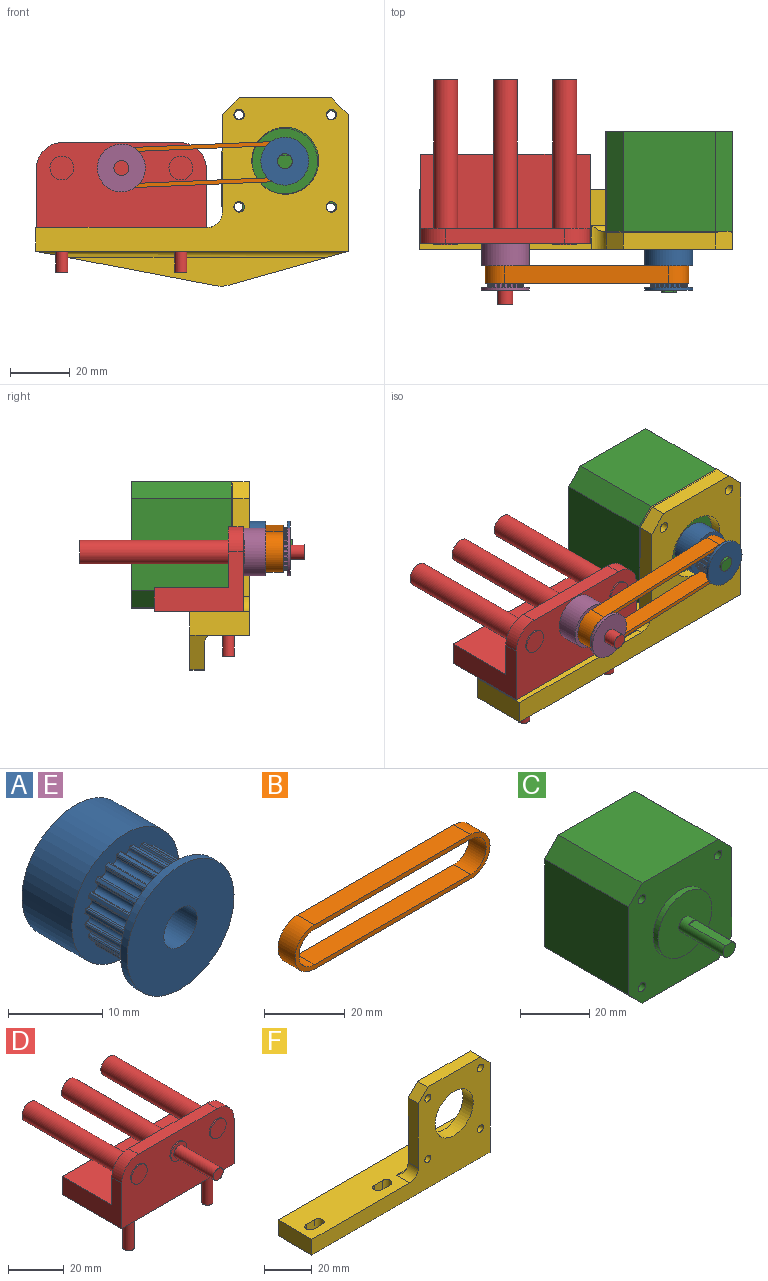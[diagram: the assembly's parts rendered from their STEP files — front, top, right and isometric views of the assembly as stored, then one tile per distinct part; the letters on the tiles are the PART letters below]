
ASSEMBLY  parts=6 mates=3
PART A: 127 faces, bbox 16.1x15.8x16.1 mm
  f0: cylinder r=2.5mm len=15.8mm, axis (0,1,0), area 248.2mm2, adj f3,f125
  f1: cylinder r=8.05mm len=16.1mm, axis (0,1,0), area 379.3mm2, adj f2,f3
  f2: plane 16.1x16.1mm, normal (0,-1,0), area 100.5mm2, adj f1,f4,f5,f6,f7,f8,f9,f10
  f3: plane 16.1x16.1mm, normal (0,1,0), area 183.9mm2, adj f0,f1
  f4: cylinder r=1mm len=7.3mm, axis (0,1,0), area 1.9mm2, adj f2,f5,f123,f126
  f5: cylinder r=0.15mm len=7.3mm, axis (0,1,0), area 1.7mm2, adj f2,f4,f6,f126
  f6: cylinder r=6.12mm len=7.3mm, axis (0,1,0), area 3mm2, adj f2,f5,f7,f126
  f7: cylinder r=0.15mm len=7.3mm, axis (0,1,0), area 1.7mm2, adj f2,f6,f8,f126
  f8: cylinder r=1mm len=7.3mm, axis (0,1,0), area 1.9mm2, adj f2,f7,f9,f126
  f9: cylinder r=0.56mm len=7.3mm, axis (0,1,0), area 9.5mm2, adj f2,f8,f10,f126
  f10: cylinder r=1mm len=7.3mm, axis (0,1,0), area 1.9mm2, adj f2,f9,f11,f126
  f11: cylinder r=0.15mm len=7.3mm, axis (0,1,0), area 1.7mm2, adj f2,f10,f12,f126
  f12: cylinder r=6.12mm len=7.3mm, axis (0,1,0), area 3mm2, adj f2,f11,f13,f126
  f13: cylinder r=0.15mm len=7.3mm, axis (0,1,0), area 1.7mm2, adj f2,f12,f14,f126
  f14: cylinder r=1mm len=7.3mm, axis (0,1,0), area 1.9mm2, adj f2,f13,f15,f126
  f15: cylinder r=0.56mm len=7.3mm, axis (0,1,0), area 9.5mm2, adj f2,f14,f16,f126
  f16: cylinder r=1mm len=7.3mm, axis (0,1,0), area 1.9mm2, adj f2,f15,f17,f126
  f17: cylinder r=0.15mm len=7.3mm, axis (0,1,0), area 1.7mm2, adj f2,f16,f18,f126
  f18: cylinder r=6.12mm len=7.3mm, axis (0,1,0), area 3mm2, adj f2,f17,f19,f126
  f19: cylinder r=0.15mm len=7.3mm, axis (0,1,0), area 1.7mm2, adj f2,f18,f20,f126
  f20: cylinder r=1mm len=7.3mm, axis (0,1,0), area 1.9mm2, adj f2,f19,f21,f126
  f21: cylinder r=0.56mm len=7.3mm, axis (0,1,0), area 9.5mm2, adj f2,f20,f22,f126
  f22: cylinder r=1mm len=7.3mm, axis (0,1,0), area 1.9mm2, adj f2,f21,f23,f126
  f23: cylinder r=0.15mm len=7.3mm, axis (0,1,0), area 1.7mm2, adj f2,f22,f24,f126
  f24: cylinder r=6.12mm len=7.3mm, axis (0,1,0), area 3mm2, adj f2,f23,f25,f126
  f25: cylinder r=0.15mm len=7.3mm, axis (0,1,0), area 1.7mm2, adj f2,f24,f26,f126
  f26: cylinder r=1mm len=7.3mm, axis (0,1,0), area 1.9mm2, adj f2,f25,f27,f126
  f27: cylinder r=0.56mm len=7.3mm, axis (0,1,0), area 9.5mm2, adj f2,f26,f28,f126
  f28: cylinder r=1mm len=7.3mm, axis (0,1,0), area 1.9mm2, adj f2,f27,f29,f126
  f29: cylinder r=0.15mm len=7.3mm, axis (0,1,0), area 1.7mm2, adj f2,f28,f30,f126
  f30: cylinder r=6.12mm len=7.3mm, axis (0,1,0), area 3mm2, adj f2,f29,f31,f126
  f31: cylinder r=0.15mm len=7.3mm, axis (0,1,0), area 1.7mm2, adj f2,f30,f32,f126
  f32: cylinder r=1mm len=7.3mm, axis (0,1,0), area 1.9mm2, adj f2,f31,f33,f126
  f33: cylinder r=0.56mm len=7.3mm, axis (0,1,0), area 9.5mm2, adj f2,f32,f34,f126
  f34: cylinder r=1mm len=7.3mm, axis (0,1,0), area 1.9mm2, adj f2,f33,f35,f126
  f35: cylinder r=0.15mm len=7.3mm, axis (0,1,0), area 1.7mm2, adj f2,f34,f36,f126
  f36: cylinder r=6.12mm len=7.3mm, axis (0,1,0), area 3mm2, adj f2,f35,f37,f126
  f37: cylinder r=0.15mm len=7.3mm, axis (0,1,0), area 1.7mm2, adj f2,f36,f38,f126
  f38: cylinder r=1mm len=7.3mm, axis (0,1,0), area 1.9mm2, adj f2,f37,f39,f126
  f39: cylinder r=0.56mm len=7.3mm, axis (0,1,0), area 9.5mm2, adj f2,f38,f40,f126
  f40: cylinder r=1mm len=7.3mm, axis (0,1,0), area 1.9mm2, adj f2,f39,f41,f126
  f41: cylinder r=0.15mm len=7.3mm, axis (0,1,0), area 1.7mm2, adj f2,f40,f42,f126
  f42: cylinder r=6.12mm len=7.3mm, axis (0,1,0), area 3mm2, adj f2,f41,f43,f126
  f43: cylinder r=0.15mm len=7.3mm, axis (0,1,0), area 1.7mm2, adj f2,f42,f44,f126
  f44: cylinder r=1mm len=7.3mm, axis (0,1,0), area 1.9mm2, adj f2,f43,f45,f126
  f45: cylinder r=0.56mm len=7.3mm, axis (0,1,0), area 9.5mm2, adj f2,f44,f46,f126
  f46: cylinder r=1mm len=7.3mm, axis (0,1,0), area 1.9mm2, adj f2,f45,f47,f126
  f47: cylinder r=0.15mm len=7.3mm, axis (0,1,0), area 1.7mm2, adj f2,f46,f48,f126
  f48: cylinder r=6.12mm len=7.3mm, axis (0,1,0), area 3mm2, adj f2,f47,f49,f126
  f49: cylinder r=0.15mm len=7.3mm, axis (0,1,0), area 1.7mm2, adj f2,f48,f50,f126
  f50: cylinder r=1mm len=7.3mm, axis (0,1,0), area 1.9mm2, adj f2,f49,f51,f126
  f51: cylinder r=0.56mm len=7.3mm, axis (0,1,0), area 9.5mm2, adj f2,f50,f52,f126
  f52: cylinder r=1mm len=7.3mm, axis (0,1,0), area 1.9mm2, adj f2,f51,f53,f126
  f53: cylinder r=0.15mm len=7.3mm, axis (0,1,0), area 1.7mm2, adj f2,f52,f54,f126
  f54: cylinder r=6.12mm len=7.3mm, axis (0,1,0), area 3mm2, adj f2,f53,f55,f126
  f55: cylinder r=0.15mm len=7.3mm, axis (0,1,0), area 1.7mm2, adj f2,f54,f56,f126
  f56: cylinder r=1mm len=7.3mm, axis (0,1,0), area 1.9mm2, adj f2,f55,f57,f126
  f57: cylinder r=0.56mm len=7.3mm, axis (0,1,0), area 9.5mm2, adj f2,f56,f58,f126
  f58: cylinder r=1mm len=7.3mm, axis (0,1,0), area 1.9mm2, adj f2,f57,f59,f126
  f59: cylinder r=0.15mm len=7.3mm, axis (0,1,0), area 1.7mm2, adj f2,f58,f60,f126
  f60: cylinder r=6.12mm len=7.3mm, axis (0,1,0), area 3mm2, adj f2,f59,f61,f126
  f61: cylinder r=0.15mm len=7.3mm, axis (0,1,0), area 1.7mm2, adj f2,f60,f62,f126
  f62: cylinder r=1mm len=7.3mm, axis (0,1,0), area 1.9mm2, adj f2,f61,f63,f126
  f63: cylinder r=0.56mm len=7.3mm, axis (0,1,0), area 9.5mm2, adj f2,f62,f64,f126
  f64: cylinder r=1mm len=7.3mm, axis (0,1,0), area 1.9mm2, adj f2,f63,f65,f126
  f65: cylinder r=0.15mm len=7.3mm, axis (0,1,0), area 1.7mm2, adj f2,f64,f66,f126
  f66: cylinder r=6.12mm len=7.3mm, axis (0,1,0), area 3mm2, adj f2,f65,f67,f126
  f67: cylinder r=0.15mm len=7.3mm, axis (0,1,0), area 1.7mm2, adj f2,f66,f68,f126
  f68: cylinder r=1mm len=7.3mm, axis (0,1,0), area 1.9mm2, adj f2,f67,f69,f126
  f69: cylinder r=0.56mm len=7.3mm, axis (0,1,0), area 9.5mm2, adj f2,f68,f70,f126
  f70: cylinder r=1mm len=7.3mm, axis (0,1,0), area 1.9mm2, adj f2,f69,f71,f126
  f71: cylinder r=0.15mm len=7.3mm, axis (0,1,0), area 1.7mm2, adj f2,f70,f72,f126
  f72: cylinder r=6.12mm len=7.3mm, axis (0,1,0), area 3mm2, adj f2,f71,f73,f126
  f73: cylinder r=0.15mm len=7.3mm, axis (0,1,0), area 1.7mm2, adj f2,f72,f74,f126
  f74: cylinder r=1mm len=7.3mm, axis (0,1,0), area 1.9mm2, adj f2,f73,f75,f126
  f75: cylinder r=0.56mm len=7.3mm, axis (0,1,0), area 9.5mm2, adj f2,f74,f76,f126
  f76: cylinder r=1mm len=7.3mm, axis (0,1,0), area 1.9mm2, adj f2,f75,f77,f126
  f77: cylinder r=0.15mm len=7.3mm, axis (0,1,0), area 1.7mm2, adj f2,f76,f78,f126
  f78: cylinder r=6.12mm len=7.3mm, axis (0,1,0), area 3mm2, adj f2,f77,f79,f126
  f79: cylinder r=0.15mm len=7.3mm, axis (0,1,0), area 1.7mm2, adj f2,f78,f80,f126
  f80: cylinder r=1mm len=7.3mm, axis (0,1,0), area 1.9mm2, adj f2,f79,f81,f126
  f81: cylinder r=0.56mm len=7.3mm, axis (0,1,0), area 9.5mm2, adj f2,f80,f82,f126
  f82: cylinder r=1mm len=7.3mm, axis (0,1,0), area 1.9mm2, adj f2,f81,f83,f126
  f83: cylinder r=0.15mm len=7.3mm, axis (0,1,0), area 1.7mm2, adj f2,f82,f84,f126
  f84: cylinder r=6.12mm len=7.3mm, axis (0,1,0), area 3mm2, adj f2,f83,f85,f126
  f85: cylinder r=0.15mm len=7.3mm, axis (0,1,0), area 1.7mm2, adj f2,f84,f86,f126
  f86: cylinder r=1mm len=7.3mm, axis (0,1,0), area 1.9mm2, adj f2,f85,f87,f126
  f87: cylinder r=0.56mm len=7.3mm, axis (0,1,0), area 9.5mm2, adj f2,f86,f88,f126
  f88: cylinder r=1mm len=7.3mm, axis (0,1,0), area 1.9mm2, adj f2,f87,f89,f126
  f89: cylinder r=0.15mm len=7.3mm, axis (0,1,0), area 1.7mm2, adj f2,f88,f90,f126
  f90: cylinder r=6.12mm len=7.3mm, axis (0,1,0), area 3mm2, adj f2,f89,f91,f126
  f91: cylinder r=0.15mm len=7.3mm, axis (0,1,0), area 1.7mm2, adj f2,f90,f92,f126
  f92: cylinder r=1mm len=7.3mm, axis (0,1,0), area 1.9mm2, adj f2,f91,f93,f126
  f93: cylinder r=0.56mm len=7.3mm, axis (0,1,0), area 9.5mm2, adj f2,f92,f94,f126
  f94: cylinder r=1mm len=7.3mm, axis (0,1,0), area 1.9mm2, adj f2,f93,f95,f126
  f95: cylinder r=0.15mm len=7.3mm, axis (0,1,0), area 1.7mm2, adj f2,f94,f96,f126
  f96: cylinder r=6.12mm len=7.3mm, axis (0,1,0), area 3mm2, adj f2,f95,f97,f126
  f97: cylinder r=0.15mm len=7.3mm, axis (0,1,0), area 1.7mm2, adj f2,f96,f98,f126
  f98: cylinder r=1mm len=7.3mm, axis (0,1,0), area 1.9mm2, adj f2,f97,f99,f126
  f99: cylinder r=0.56mm len=7.3mm, axis (0,1,0), area 9.5mm2, adj f2,f98,f100,f126
  f100: cylinder r=1mm len=7.3mm, axis (0,1,0), area 1.9mm2, adj f2,f99,f101,f126
  f101: cylinder r=0.15mm len=7.3mm, axis (0,1,0), area 1.7mm2, adj f2,f100,f102,f126
  f102: cylinder r=6.12mm len=7.3mm, axis (0,1,0), area 3mm2, adj f2,f101,f103,f126
  f103: cylinder r=0.15mm len=7.3mm, axis (0,1,0), area 1.7mm2, adj f2,f102,f104,f126
  f104: cylinder r=1mm len=7.3mm, axis (0,1,0), area 1.9mm2, adj f2,f103,f105,f126
  f105: cylinder r=0.56mm len=7.3mm, axis (0,1,0), area 9.5mm2, adj f2,f104,f106,f126
  f106: cylinder r=1mm len=7.3mm, axis (0,1,0), area 1.9mm2, adj f2,f105,f107,f126
  f107: cylinder r=0.15mm len=7.3mm, axis (0,1,0), area 1.7mm2, adj f2,f106,f108,f126
  f108: cylinder r=6.12mm len=7.3mm, axis (0,1,0), area 3mm2, adj f2,f107,f109,f126
  f109: cylinder r=0.15mm len=7.3mm, axis (0,1,0), area 1.7mm2, adj f2,f108,f110,f126
  f110: cylinder r=1mm len=7.3mm, axis (0,1,0), area 1.9mm2, adj f2,f109,f111,f126
  f111: cylinder r=0.56mm len=7.3mm, axis (0,1,0), area 9.5mm2, adj f2,f110,f112,f126
  f112: cylinder r=1mm len=7.3mm, axis (0,1,0), area 1.9mm2, adj f2,f111,f113,f126
  f113: cylinder r=0.15mm len=7.3mm, axis (0,1,0), area 1.7mm2, adj f2,f112,f114,f126
  f114: cylinder r=6.12mm len=7.3mm, axis (0,1,0), area 3mm2, adj f2,f113,f115,f126
  f115: cylinder r=0.15mm len=7.3mm, axis (0,1,0), area 1.7mm2, adj f2,f114,f116,f126
  f116: cylinder r=1mm len=7.3mm, axis (0,1,0), area 1.9mm2, adj f2,f115,f117,f126
  f117: cylinder r=0.56mm len=7.3mm, axis (0,1,0), area 9.5mm2, adj f2,f116,f118,f126
  f118: cylinder r=1mm len=7.3mm, axis (0,1,0), area 1.9mm2, adj f2,f117,f119,f126
  f119: cylinder r=0.15mm len=7.3mm, axis (0,1,0), area 1.7mm2, adj f2,f118,f120,f126
  f120: cylinder r=6.12mm len=7.3mm, axis (0,1,0), area 3mm2, adj f2,f119,f121,f126
  f121: cylinder r=0.15mm len=7.3mm, axis (0,1,0), area 1.7mm2, adj f2,f120,f122,f126
  f122: cylinder r=1mm len=7.3mm, axis (0,1,0), area 1.9mm2, adj f2,f121,f123,f126
  f123: cylinder r=0.56mm len=7.3mm, axis (0,1,0), area 9.5mm2, adj f2,f4,f122,f126
  f124: cylinder r=8.05mm len=16.1mm, axis (0,1,0), area 50.6mm2, adj f125,f126
  f125: plane 16.1x16.1mm, normal (0,-1,0), area 183.9mm2, adj f0,f124
  f126: plane 16.1x16.1mm, normal (0,1,0), area 100.5mm2, adj f4,f5,f6,f7,f8,f9,f10,f11
PART B: 10 faces, bbox 68.5x6x13.5 mm
  f0: plane 55x6mm, normal (0,0,1), area 330mm2, adj f1,f7,f8,f9
  f1: cylinder r=5.37mm len=10.73mm, axis (0,1,0), area 101.1mm2, adj f0,f2,f8,f9
  f2: plane 55x6mm, normal (0,0,-1), area 330mm2, adj f1,f7,f8,f9
  f3: cylinder r=6.75mm len=13.49mm, axis (0,1,0), area 127.1mm2, adj f4,f6,f8,f9
  f4: plane 55x6mm, normal (0,0,-1), area 330mm2, adj f3,f5,f8,f9
  f5: cylinder r=6.75mm len=13.49mm, axis (0,1,0), area 127.1mm2, adj f4,f6,f8,f9
  f6: plane 55x6mm, normal (0,0,1), area 330mm2, adj f3,f5,f8,f9
  f7: cylinder r=5.37mm len=10.73mm, axis (0,1,0), area 101.1mm2, adj f0,f2,f8,f9
  f8: plane 68.49x13.49mm, normal (0,-1,0), area 204.3mm2, adj f0,f1,f2,f3,f4,f5,f6,f7
  f9: plane 68.49x13.49mm, normal (0,1,0), area 204.3mm2, adj f0,f1,f2,f3,f4,f5,f6,f7
PART C: 20 faces, bbox 42.3x54x42.3 mm
  f0: cylinder r=11mm len=22mm, axis (0,1,0), area 138.2mm2, adj f1,f18
  f1: plane 22x22mm, normal (0,-1,0), area 360.5mm2, adj f0,f3
  f2: plane 15x3mm, normal (0,0,1), area 45mm2, adj f3,f4,f5
  f3: cylinder r=2.5mm len=18mm, axis (0,1,0), area 234.5mm2, adj f1,f2,f4,f5
  f4: plane 5x4.5mm, normal (0,-1,0), area 18.6mm2, adj f2,f3
  f5: plane 3x0.5mm, normal (0,-1,0), area 1mm2, adj f2,f3
  f6: plane 34x31mm, normal (0,0,-1), area 1054mm2, adj f7,f16,f18,f19
  f7: plane 34x5.65mm, normal (0.71,0,-0.71), area 271.7mm2, adj f6,f8,f18,f19
  f8: plane 34x31mm, normal (1,0,0), area 1054mm2, adj f7,f9,f18,f19
  f9: plane 34x5.65mm, normal (0.71,0,0.71), area 271.7mm2, adj f8,f10,f18,f19
  f10: plane 34x31mm, normal (0,0,1), area 1054mm2, adj f9,f11,f18,f19
  f11: plane 34x5.65mm, normal (-0.71,0,0.71), area 271.7mm2, adj f10,f12,f18,f19
  f12: plane 34x31mm, normal (-1,0,0), area 1054mm2, adj f11,f16,f18,f19
  f13: cylinder r=1.5mm len=34mm, axis (0,-1,0), area 320.4mm2, adj f18,f19
  f14: cylinder r=1.5mm len=34mm, axis (0,-1,0), area 320.4mm2, adj f18,f19
  f15: cylinder r=1.5mm len=34mm, axis (0,-1,0), area 320.4mm2, adj f18,f19
  f16: plane 34x5.65mm, normal (-0.71,0,-0.71), area 271.7mm2, adj f6,f12,f18,f19
  f17: cylinder r=1.5mm len=34mm, axis (0,-1,0), area 320.4mm2, adj f18,f19
  f18: plane 42.3x42.3mm, normal (0,-1,0), area 1317mm2, adj f0,f6,f7,f8,f9,f10,f11,f12
  f19: plane 42.3x42.3mm, normal (0,1,0), area 1697.2mm2, adj f6,f7,f8,f9,f10,f11,f12,f13
PART D: 28 faces, bbox 57x75.5x43.5 mm
  f0: plane 57x30mm, normal (0,0,-1), area 1684.9mm2, adj f1,f5,f6,f21,f22,f24
  f1: plane 30x20mm, normal (1,0,0), area 300mm2, adj f0,f2,f6,f7,f20,f21
  f2: cylinder r=8.5mm len=8.5mm, axis (0,1,0), area 66.8mm2, adj f1,f3,f6,f7
  f3: plane 40x5mm, normal (0,0,1), area 200mm2, adj f2,f4,f6,f7
  f4: cylinder r=8.5mm len=8.5mm, axis (0,1,0), area 66.8mm2, adj f3,f5,f6,f7
  f5: plane 30x20mm, normal (-1,0,0), area 300mm2, adj f0,f4,f6,f7,f20,f21
  f6: plane 57x28.5mm, normal (0,-1,0), area 1442.7mm2, adj f0,f1,f2,f3,f4,f5,f10,f14
  f7: plane 57x20.5mm, normal (0,1,0), area 986.7mm2, adj f1,f2,f3,f4,f5,f9,f13,f17
  f8: plane 8x8mm, normal (0,1,0), area 50.3mm2, adj f9
  f9: cylinder r=4mm len=50mm, axis (0,-1,0), area 1256.6mm2, adj f7,f8
  f10: cylinder r=4mm len=8mm, axis (0,-1,0), area 12.6mm2, adj f6,f11
  f11: plane 8x8mm, normal (0,-1,0), area 30.6mm2, adj f10,f26
  f12: plane 8x8mm, normal (0,1,0), area 50.3mm2, adj f13
  f13: cylinder r=4mm len=50mm, axis (0,-1,0), area 1256.6mm2, adj f7,f12
  f14: cylinder r=4mm len=8mm, axis (0,-1,0), area 12.6mm2, adj f6,f15
  f15: plane 8x8mm, normal (0,-1,0), area 50.3mm2, adj f14
  f16: plane 8x8mm, normal (0,1,0), area 50.3mm2, adj f17
  f17: cylinder r=4mm len=50mm, axis (0,-1,0), area 1256.6mm2, adj f7,f16
  f18: cylinder r=4mm len=8mm, axis (0,-1,0), area 12.6mm2, adj f6,f19
  f19: plane 8x8mm, normal (0,-1,0), area 50.3mm2, adj f18
  f20: plane 57x25mm, normal (0,0,1), area 1425mm2, adj f1,f5,f7,f21
  f21: plane 57x8mm, normal (0,1,0), area 456mm2, adj f0,f1,f5,f20
  f22: cylinder r=2mm len=15mm, axis (0,0,1), area 188.5mm2, adj f0,f23
  f23: plane 4x4mm, normal (0,0,-1), area 12.6mm2, adj f22
  f24: cylinder r=2mm len=15mm, axis (0,0,1), area 188.5mm2, adj f0,f25
  f25: plane 4x4mm, normal (0,0,-1), area 12.6mm2, adj f24
  f26: cylinder r=2.5mm len=20mm, axis (0,1,0), area 314.2mm2, adj f11,f27
  f27: plane 5x5mm, normal (0,-1,0), area 19.6mm2, adj f26
PART E: same geometry as A
PART F: 31 faces, bbox 105x20x63.3 mm
  f0: plane 105x13mm, normal (0,0,-1), area 1288.2mm2, adj f3,f5,f6,f7,f8,f9,f10,f11
  f1: plane 32.93x6mm, normal (-1,0,0), area 197.6mm2, adj f16,f22,f23,f24
  f2: plane 105x20mm, normal (0,0,1), area 1644.8mm2, adj f3,f4,f5,f6,f7,f8,f9,f10
  f3: plane 45.93x20mm, normal (1,0,0), area 388.4mm2, adj f0,f2,f4,f14,f22,f23,f25,f26
  f4: plane 105x19.73mm, normal (0,1,0), area 1469.6mm2, adj f2,f3,f13,f26,f27,f28
  f5: cylinder r=2.25mm len=8mm, axis (0,0,-1), area 56.5mm2, adj f0,f2,f6,f11
  f6: plane 8x5mm, normal (0,-1,0), area 40mm2, adj f0,f2,f5,f7
  f7: cylinder r=2.25mm len=8mm, axis (0,0,-1), area 56.5mm2, adj f0,f2,f6,f11
  f8: cylinder r=2.25mm len=8mm, axis (0,0,-1), area 56.5mm2, adj f0,f2,f9,f12
  f9: plane 8x5mm, normal (0,-1,0), area 40mm2, adj f0,f2,f8,f10
  f10: cylinder r=2.25mm len=8mm, axis (0,0,-1), area 56.5mm2, adj f0,f2,f9,f12
  f11: plane 8x5mm, normal (0,1,0), area 40mm2, adj f0,f2,f5,f7
  f12: plane 8x5mm, normal (0,1,0), area 40mm2, adj f0,f2,f8,f10
  f13: plane 20x8mm, normal (-1,0,0), area 160mm2, adj f0,f2,f4,f22,f28
  f14: plane 6x5.65mm, normal (0.71,0,0.71), area 47.9mm2, adj f3,f15,f22,f23
  f15: plane 31x6mm, normal (0,0,1), area 186mm2, adj f14,f16,f22,f23
  f16: plane 6x5.65mm, normal (-0.71,0,0.71), area 47.9mm2, adj f1,f15,f22,f23
  f17: cylinder r=1.75mm len=6mm, axis (0,1,0), area 66mm2, adj f22,f23
  f18: cylinder r=1.75mm len=6mm, axis (0,1,0), area 66mm2, adj f22,f23
  f19: cylinder r=1.75mm len=6mm, axis (0,1,0), area 66mm2, adj f22,f23
  f20: cylinder r=1.75mm len=6mm, axis (0,1,0), area 66mm2, adj f22,f23
  f21: cylinder r=11.25mm len=22.5mm, axis (0,1,0), area 424.1mm2, adj f22,f23
  f22: plane 105x51.58mm, normal (0,-1,0), area 2220.6mm2, adj f0,f1,f2,f3,f13,f14,f15,f16
  f23: plane 43.3x41.58mm, normal (0,1,0), area 1291.6mm2, adj f1,f3,f14,f15,f16,f17,f18,f19
  f24: cylinder r=5mm len=8mm, axis (0,1,0), area 50.7mm2, adj f1,f2,f22,f23,f25
  f25: cylinder r=2mm len=47.3mm, axis (1,0,0), area 141.6mm2, adj f2,f3,f23,f24
  f26: plane 40.02x11.35mm, normal (0.27,0,-0.96), area 211.1mm2, adj f3,f4,f27,f29,f30
  f27: cylinder r=10mm len=5mm, axis (0,1,0), area 23.3mm2, adj f4,f26,f28,f29
  f28: plane 60.37x11.55mm, normal (-0.19,0,-0.98), area 311.9mm2, adj f4,f13,f27,f29,f30
  f29: plane 87.5x9.73mm, normal (0,-1,0), area 437.1mm2, adj f26,f27,f28,f30
  f30: cylinder r=2mm len=105mm, axis (1,0,0), area 309.9mm2, adj f0,f26,f28,f29
PLACE A rot(axis=(0,-1,0),32.4deg) t=(54.95,-5,2.28)mm
PLACE B rot(axis=(0,-1,0),2.4deg) t=(0,-12.5,0)mm
PLACE C rot(axis=(0,1,0),0.3deg) t=(54.95,-1.5,2.28)mm
PLACE D at identity fixed
PLACE E rot(axis=(0,1,0),57.6deg) t=(0,-5,0)mm
PLACE F t=(55.09,13,-28)mm
MATE revolute D.f9 <-> E.f1  axis (0,-1,0) through (0,-5,0)mm
MATE pin_slot F.f2 <-> D.f24  axis (0,0,1) through (19.74,0,-20)mm
MATE pin_slot F.f2 <-> D.f22  axis (0,0,1) through (-20.26,0,-20)mm
